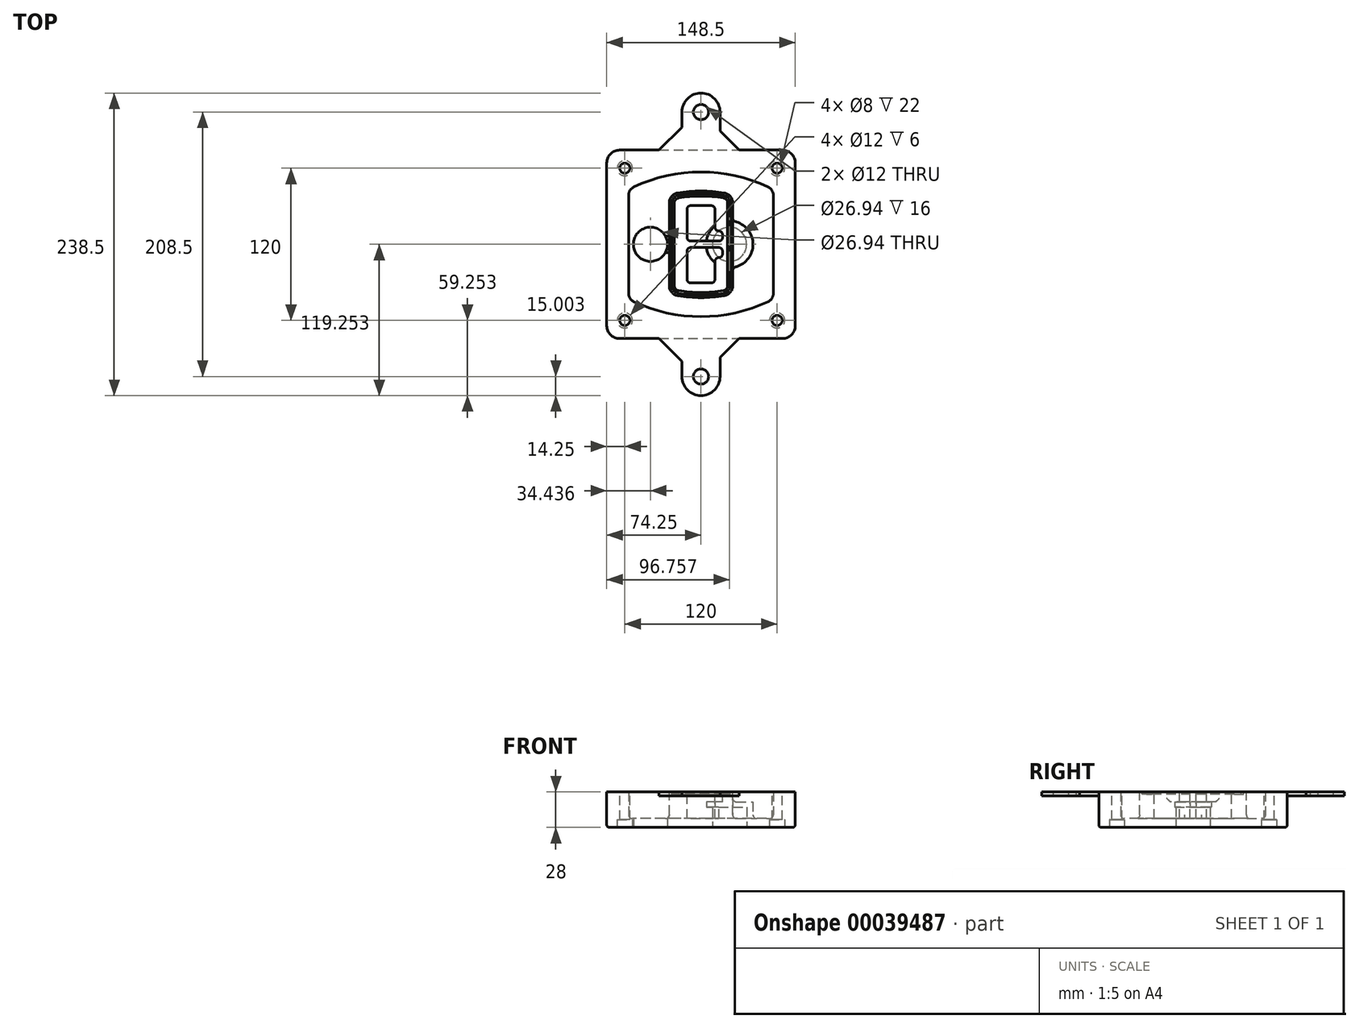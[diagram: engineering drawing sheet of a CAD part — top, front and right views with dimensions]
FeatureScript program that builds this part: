
annotation { "Feature Type Name" : "Feature", "Feature Type Description" : "" }
export const myFeature = defineFeature(function(context is Context, id is Id, definition is map)
    precondition{}
    {
        {
            var Q0;
            Q0=qCreatedBy(makeId("Top.planeOp"),FACE);
            var sketch = newSketch(context, id + "F0", { "sketchPlane" : qUnion([Q0])});
            skPoint(sketch, "E0.rect.middle", {"position": v(0, 0) * mm});
            skLineSegment(sketch, "E1.bottom", {"start": v(24.05, 28.38) * mm, "end": v(152.55, 28.38) * mm});
            skLineSegment(sketch, "E1.top", {"start": v(24.05, 176.88) * mm, "end": v(152.55, 176.88) * mm});
            skLineSegment(sketch, "E1.left", {"start": v(14.05, 38.38) * mm, "end": v(14.05, 166.88) * mm});
            skLineSegment(sketch, "E1.right", {"start": v(162.55, 38.38) * mm, "end": v(162.55, 166.88) * mm});
            skLineSegment(sketch, "E2", {"start": v(14.05, 176.88) * mm, "end": v(162.55, 28.38) * mm, "construction": true});
            skLineSegment(sketch, "E3", {"start": v(162.55, 176.88) * mm, "end": v(14.05, 28.38) * mm, "construction": true});
            skCircle(sketch, "E4", {"center": v(28.3, 162.63) * mm, "radius": 4 * mm});
            skCircle(sketch, "E5", {"center": v(148.3, 162.63) * mm, "radius": 4 * mm});
            skCircle(sketch, "E6", {"center": v(148.3, 42.63) * mm, "radius": 4 * mm});
            skCircle(sketch, "E7", {"center": v(28.3, 42.63) * mm, "radius": 4 * mm});
            skLineSegment(sketch, "E8", {"start": v(28.3, 162.63) * mm, "end": v(148.3, 162.63) * mm, "construction": true});
            skLineSegment(sketch, "E9", {"start": v(148.3, 162.63) * mm, "end": v(148.3, 42.63) * mm, "construction": true});
            skLineSegment(sketch, "E10", {"start": v(148.3, 42.63) * mm, "end": v(28.3, 42.63) * mm, "construction": true});
            skLineSegment(sketch, "E11", {"start": v(28.3, 42.63) * mm, "end": v(28.3, 162.63) * mm, "construction": true});
            skLineSegment(sketch, "E12", {"start": v(28.3, 141.46) * mm, "end": v(28.3, 63.8) * mm});
            skLineSegment(sketch, "E13", {"start": v(148.3, 141.46) * mm, "end": v(148.3, 63.8) * mm});
            skArc(sketch, "E14", {"start": v(142.56, 150.51) * mm, "mid": v(88.3, 162.63) * mm, "end": v(34.04, 150.51) * mm});
            skArc(sketch, "E15", {"start": v(34.04, 54.75) * mm, "mid": v(88.3, 42.63) * mm, "end": v(142.56, 54.75) * mm});
            skLineSegment(sketch, "E16", {"start": v(28.3, 102.63) * mm, "end": v(148.3, 102.63) * mm, "construction": true});
            skPoint(sketch, "E17.visualSharp", {"position": v(28.3, 57.63) * mm});
            skArc(sketch, "E17.filletArc", {"start": v(28.3, 63.8) * mm, "mid": v(29.86, 58.44) * mm, "end": v(34.04, 54.75) * mm});
            skPoint(sketch, "E18.visualSharp", {"position": v(28.3, 147.63) * mm});
            skArc(sketch, "E18.filletArc", {"start": v(34.04, 150.51) * mm, "mid": v(29.86, 146.82) * mm, "end": v(28.3, 141.46) * mm});
            skPoint(sketch, "E19.visualSharp", {"position": v(148.3, 147.63) * mm});
            skArc(sketch, "E19.filletArc", {"start": v(148.3, 141.46) * mm, "mid": v(146.74, 146.82) * mm, "end": v(142.56, 150.51) * mm});
            skPoint(sketch, "E20.visualSharp", {"position": v(148.3, 57.63) * mm});
            skArc(sketch, "E20.filletArc", {"start": v(142.56, 54.75) * mm, "mid": v(146.74, 58.44) * mm, "end": v(148.3, 63.8) * mm});
            skPoint(sketch, "E21.visualSharp", {"position": v(14.05, 176.88) * mm});
            skArc(sketch, "E21.filletArc", {"start": v(24.05, 176.88) * mm, "mid": v(16.98, 173.95) * mm, "end": v(14.05, 166.88) * mm});
            skPoint(sketch, "E22.visualSharp", {"position": v(162.55, 176.88) * mm});
            skArc(sketch, "E22.filletArc", {"start": v(162.55, 166.88) * mm, "mid": v(159.62, 173.95) * mm, "end": v(152.55, 176.88) * mm});
            skPoint(sketch, "E23.visualSharp", {"position": v(162.55, 28.38) * mm});
            skArc(sketch, "E23.filletArc", {"start": v(152.55, 28.38) * mm, "mid": v(159.62, 31.31) * mm, "end": v(162.55, 38.38) * mm});
            skPoint(sketch, "E24.visualSharp", {"position": v(14.05, 28.38) * mm});
            skArc(sketch, "E24.filletArc", {"start": v(14.05, 38.38) * mm, "mid": v(16.98, 31.31) * mm, "end": v(24.05, 28.38) * mm});
            skArc(sketch, "E25.0", {"start": v(145.3, 141.46) * mm, "mid": v(144.2, 145.22) * mm, "end": v(141.28, 147.8) * mm});
            skLineSegment(sketch, "E25.1", {"start": v(145.3, 141.46) * mm, "end": v(145.3, 63.8) * mm});
            skArc(sketch, "E25.2", {"start": v(141.28, 57.47) * mm, "mid": v(144.2, 60.05) * mm, "end": v(145.3, 63.8) * mm});
            skArc(sketch, "E25.3", {"start": v(35.32, 57.47) * mm, "mid": v(88.3, 45.63) * mm, "end": v(141.28, 57.47) * mm});
            skArc(sketch, "E25.4", {"start": v(31.3, 63.8) * mm, "mid": v(32.4, 60.05) * mm, "end": v(35.32, 57.47) * mm});
            skArc(sketch, "E25.5", {"start": v(141.28, 147.8) * mm, "mid": v(88.3, 159.63) * mm, "end": v(35.32, 147.8) * mm});
            skLineSegment(sketch, "E25.6", {"start": v(31.3, 141.46) * mm, "end": v(31.3, 63.8) * mm});
            skArc(sketch, "E25.7", {"start": v(35.32, 147.8) * mm, "mid": v(32.4, 145.22) * mm, "end": v(31.3, 141.46) * mm});
            skArc(sketch, "E26.0", {"start": v(32.34, 154.13) * mm, "mid": v(26.48, 148.97) * mm, "end": v(24.3, 141.46) * mm});
            skArc(sketch, "E26.1", {"start": v(144.26, 154.13) * mm, "mid": v(88.3, 166.63) * mm, "end": v(32.34, 154.13) * mm});
            skArc(sketch, "E26.2", {"start": v(152.3, 141.46) * mm, "mid": v(150.12, 148.97) * mm, "end": v(144.26, 154.13) * mm});
            skLineSegment(sketch, "E26.3", {"start": v(152.3, 141.46) * mm, "end": v(152.3, 63.8) * mm});
            skArc(sketch, "E26.4", {"start": v(144.26, 51.13) * mm, "mid": v(150.12, 56.3) * mm, "end": v(152.3, 63.8) * mm});
            skLineSegment(sketch, "E26.5", {"start": v(24.3, 141.46) * mm, "end": v(24.3, 63.8) * mm});
            skArc(sketch, "E26.6", {"start": v(32.34, 51.13) * mm, "mid": v(88.3, 38.63) * mm, "end": v(144.26, 51.13) * mm});
            skArc(sketch, "E26.7", {"start": v(24.3, 63.8) * mm, "mid": v(26.48, 56.3) * mm, "end": v(32.34, 51.13) * mm});
            skSolve(sketch);
        }
        {
            var Q0;
            Q0=makeQuery(id+"F0.imprint","IMPRINT",FACE,{"disambiguationData":[TD([[makeQuery(id+"F0.imprint","IMPRINT",EDGE,{"derivedFrom":sQuery(id+"F0.wireOp",EDGE,"E1.bottom")}),1.0]])]});
            var Q1;
            Q1=makeQuery(id+"F0.imprint","IMPRINT",FACE,{"disambiguationData":[TD([[makeQuery(id+"F0.imprint","IMPRINT",EDGE,{"derivedFrom":sQuery(id+"F0.wireOp",EDGE,"E12")}),1.0]])]});
            var Q2;
            Q2=makeQuery(id+"F0.imprint","IMPRINT",FACE,{"disambiguationData":[TD([[makeQuery(id+"F0.imprint","IMPRINT",EDGE,{"derivedFrom":sQuery(id+"F0.wireOp",EDGE,"E25.0")}),1.0]])]});
            var Q3;
            Q3=makeQuery(id+"F0.imprint","IMPRINT",FACE,{"disambiguationData":[TD([[makeQuery(id+"F0.imprint","IMPRINT",EDGE,{"derivedFrom":sQuery(id+"F0.wireOp",EDGE,"E12")}),-1.0]])]});
            extrude(context, id + "F1", {"entities" : qUnion([Q0, Q1, Q2, Q3]), "oppositeDirection" : true, "depth" : 25 * mm});
        }
        {
            var Q0;
            Q0=makeQuery(id+"F0.imprint","IMPRINT",FACE,{"disambiguationData":[TD([[makeQuery(id+"F0.imprint","IMPRINT",EDGE,{"derivedFrom":sQuery(id+"F0.wireOp",EDGE,"E12")}),1.0]])]});
            extrude(context, id + "F2", {"entities" : qUnion([Q0]), "operationType" : NewBodyOperationType.ADD, "depth" : 3 * mm});
        }
        {
            var Q0;
            Q0=makeQuery(id+"F0.imprint","IMPRINT",FACE,{"disambiguationData":[TD([[makeQuery(id+"F0.imprint","IMPRINT",EDGE,{"derivedFrom":sQuery(id+"F0.wireOp",EDGE,"E25.0")}),1.0]])]});
            extrude(context, id + "F3", {"entities" : qUnion([Q0]), "operationType" : NewBodyOperationType.REMOVE, "oppositeDirection" : true, "depth" : 18 * mm});
        }
        {
            var Q0;
            Q0=makeQuery(id+"F2.opExtrude","CAP_FACE",FACE,{"disambiguationData":[OSD([sQuery(id+"F0.wireOp",EDGE,"E12"),sQuery(id+"F0.wireOp",EDGE,"E13"),sQuery(id+"F0.wireOp",EDGE,"E14"),sQuery(id+"F0.wireOp",EDGE,"E15"),sQuery(id+"F0.wireOp",EDGE,"E17.filletArc"),sQuery(id+"F0.wireOp",EDGE,"E18.filletArc"),sQuery(id+"F0.wireOp",EDGE,"E19.filletArc"),sQuery(id+"F0.wireOp",EDGE,"E20.filletArc"),sQuery(id+"F0.wireOp",EDGE,"E25.0"),sQuery(id+"F0.wireOp",EDGE,"E25.1"),sQuery(id+"F0.wireOp",EDGE,"E25.2"),sQuery(id+"F0.wireOp",EDGE,"E25.3"),sQuery(id+"F0.wireOp",EDGE,"E25.4"),sQuery(id+"F0.wireOp",EDGE,"E25.5"),sQuery(id+"F0.wireOp",EDGE,"E25.6"),sQuery(id+"F0.wireOp",EDGE,"E25.7")])],"isStart":false});
            var sketch = newSketch(context, id + "F4", { "sketchPlane" : qUnion([Q0])});
            skArc(sketch, "E27.0", {"start": v(69.96, 62.18) * mm, "mid": v(88.3, 60.63) * mm, "end": v(106.64, 62.18) * mm});
            skArc(sketch, "E28.0", {"start": v(106.64, 143.09) * mm, "mid": v(88.3, 144.63) * mm, "end": v(69.96, 143.09) * mm});
            skLineSegment(sketch, "E29", {"start": v(63.3, 135.2) * mm, "end": v(63.3, 70.07) * mm});
            skLineSegment(sketch, "E30", {"start": v(113.3, 135.2) * mm, "end": v(113.3, 70.07) * mm});
            skLineSegment(sketch, "E31", {"start": v(63.3, 141.74) * mm, "end": v(113.3, 141.74) * mm, "construction": true});
            skLineSegment(sketch, "E32", {"start": v(63.3, 63.52) * mm, "end": v(113.3, 63.52) * mm, "construction": true});
            skPoint(sketch, "E33.visualSharp", {"position": v(63.3, 141.74) * mm});
            skArc(sketch, "E33.filletArc", {"start": v(69.96, 143.09) * mm, "mid": v(65.19, 140.36) * mm, "end": v(63.3, 135.2) * mm});
            skPoint(sketch, "E34.visualSharp", {"position": v(113.3, 141.74) * mm});
            skArc(sketch, "E34.filletArc", {"start": v(113.3, 135.2) * mm, "mid": v(111.41, 140.36) * mm, "end": v(106.64, 143.09) * mm});
            skPoint(sketch, "E35.visualSharp", {"position": v(113.3, 63.52) * mm});
            skArc(sketch, "E35.filletArc", {"start": v(106.64, 62.18) * mm, "mid": v(111.41, 64.9) * mm, "end": v(113.3, 70.07) * mm});
            skPoint(sketch, "E36.visualSharp", {"position": v(63.3, 63.52) * mm});
            skArc(sketch, "E36.filletArc", {"start": v(63.3, 70.07) * mm, "mid": v(65.19, 64.9) * mm, "end": v(69.96, 62.18) * mm});
            skArc(sketch, "E37.0", {"start": v(141.28, 147.8) * mm, "mid": v(88.3, 159.63) * mm, "end": v(35.32, 147.8) * mm});
            skArc(sketch, "E37.1", {"start": v(35.32, 147.8) * mm, "mid": v(32.4, 145.22) * mm, "end": v(31.3, 141.46) * mm});
            skLineSegment(sketch, "E37.2", {"start": v(31.3, 141.46) * mm, "end": v(31.3, 63.8) * mm});
            skArc(sketch, "E37.3", {"start": v(31.3, 63.8) * mm, "mid": v(32.4, 60.05) * mm, "end": v(35.32, 57.47) * mm});
            skArc(sketch, "E37.4", {"start": v(35.32, 57.47) * mm, "mid": v(88.3, 45.63) * mm, "end": v(141.28, 57.47) * mm});
            skArc(sketch, "E37.5", {"start": v(141.28, 57.47) * mm, "mid": v(144.2, 60.05) * mm, "end": v(145.3, 63.8) * mm});
            skLineSegment(sketch, "E37.6", {"start": v(145.3, 141.46) * mm, "end": v(145.3, 63.8) * mm});
            skArc(sketch, "E37.7", {"start": v(145.3, 141.46) * mm, "mid": v(144.2, 145.22) * mm, "end": v(141.28, 147.8) * mm});
            skLineSegment(sketch, "E38.0", {"start": v(111.3, 135.2) * mm, "end": v(111.3, 70.07) * mm});
            skArc(sketch, "E38.1", {"start": v(106.3, 64.15) * mm, "mid": v(109.88, 66.2) * mm, "end": v(111.3, 70.07) * mm});
            skArc(sketch, "E38.2", {"start": v(70.3, 64.15) * mm, "mid": v(88.3, 62.63) * mm, "end": v(106.3, 64.15) * mm});
            skArc(sketch, "E38.3", {"start": v(65.3, 70.07) * mm, "mid": v(66.72, 66.2) * mm, "end": v(70.3, 64.15) * mm});
            skLineSegment(sketch, "E38.4", {"start": v(65.3, 135.2) * mm, "end": v(65.3, 70.07) * mm});
            skArc(sketch, "E38.5", {"start": v(111.3, 135.2) * mm, "mid": v(109.88, 139.07) * mm, "end": v(106.3, 141.11) * mm});
            skArc(sketch, "E38.6", {"start": v(70.3, 141.11) * mm, "mid": v(66.72, 139.07) * mm, "end": v(65.3, 135.2) * mm});
            skArc(sketch, "E38.7", {"start": v(106.3, 141.11) * mm, "mid": v(88.3, 142.63) * mm, "end": v(70.3, 141.11) * mm});
            skArc(sketch, "E39.0", {"start": v(109.3, 135.2) * mm, "mid": v(108.36, 137.78) * mm, "end": v(105.97, 139.14) * mm});
            skLineSegment(sketch, "E39.1", {"start": v(109.3, 135.2) * mm, "end": v(109.3, 70.07) * mm});
            skArc(sketch, "E39.2", {"start": v(105.97, 66.12) * mm, "mid": v(108.36, 67.49) * mm, "end": v(109.3, 70.07) * mm});
            skArc(sketch, "E39.3", {"start": v(70.63, 66.12) * mm, "mid": v(88.3, 64.63) * mm, "end": v(105.97, 66.12) * mm});
            skArc(sketch, "E39.4", {"start": v(67.3, 70.07) * mm, "mid": v(68.24, 67.49) * mm, "end": v(70.63, 66.12) * mm});
            skArc(sketch, "E39.5", {"start": v(105.97, 139.14) * mm, "mid": v(88.3, 140.63) * mm, "end": v(70.63, 139.14) * mm});
            skLineSegment(sketch, "E39.6", {"start": v(67.3, 135.2) * mm, "end": v(67.3, 70.07) * mm});
            skArc(sketch, "E39.7", {"start": v(70.63, 139.14) * mm, "mid": v(68.24, 137.78) * mm, "end": v(67.3, 135.2) * mm});
            skLineSegment(sketch, "E40", {"start": v(63.3, 102.63) * mm, "end": v(113.3, 102.63) * mm, "construction": true});
            skLineSegment(sketch, "E41", {"start": v(77.3, 108.13) * mm, "end": v(77.3, 130.13) * mm});
            skLineSegment(sketch, "E42", {"start": v(80.3, 133.13) * mm, "end": v(96.3, 133.13) * mm});
            skLineSegment(sketch, "E43", {"start": v(99.3, 130.13) * mm, "end": v(99.3, 116.13) * mm});
            skLineSegment(sketch, "E44", {"start": v(102.3, 113.13) * mm, "end": v(102.3, 113.13) * mm});
            skLineSegment(sketch, "E45", {"start": v(105.3, 110.13) * mm, "end": v(105.3, 108.13) * mm});
            skLineSegment(sketch, "E46", {"start": v(102.3, 105.13) * mm, "end": v(80.3, 105.13) * mm});
            skPoint(sketch, "E47.visualSharp", {"position": v(77.3, 133.13) * mm});
            skArc(sketch, "E47.filletArc", {"start": v(80.3, 133.13) * mm, "mid": v(78.18, 132.25) * mm, "end": v(77.3, 130.13) * mm});
            skPoint(sketch, "E48.visualSharp", {"position": v(99.3, 133.13) * mm});
            skArc(sketch, "E48.filletArc", {"start": v(99.3, 130.13) * mm, "mid": v(98.42, 132.25) * mm, "end": v(96.3, 133.13) * mm});
            skPoint(sketch, "E49.visualSharp", {"position": v(99.3, 113.13) * mm});
            skArc(sketch, "E49.filletArc", {"start": v(99.3, 116.13) * mm, "mid": v(100.18, 114.01) * mm, "end": v(102.3, 113.13) * mm});
            skPoint(sketch, "E50.visualSharp", {"position": v(105.3, 113.13) * mm});
            skArc(sketch, "E50.filletArc", {"start": v(105.3, 110.13) * mm, "mid": v(104.42, 112.25) * mm, "end": v(102.3, 113.13) * mm});
            skPoint(sketch, "E51.visualSharp", {"position": v(105.3, 105.13) * mm});
            skArc(sketch, "E51.filletArc", {"start": v(102.3, 105.13) * mm, "mid": v(104.42, 106.01) * mm, "end": v(105.3, 108.13) * mm});
            skPoint(sketch, "E52.visualSharp", {"position": v(77.3, 105.13) * mm});
            skArc(sketch, "E52.filletArc", {"start": v(77.3, 108.13) * mm, "mid": v(78.18, 106.01) * mm, "end": v(80.3, 105.13) * mm});
            skLineSegment(sketch, "E53.0.MirrorCS", {"start": v(102.3, 100.13) * mm, "end": v(80.3, 100.13) * mm});
            skArc(sketch, "E54.0.MirrorCS", {"start": v(77.3, 97.13) * mm, "mid": v(78.18, 99.25) * mm, "end": v(80.3, 100.13) * mm});
            skLineSegment(sketch, "E55.0.MirrorCS", {"start": v(77.3, 97.13) * mm, "end": v(77.3, 75.13) * mm});
            skArc(sketch, "E56.0.MirrorCS", {"start": v(80.3, 72.13) * mm, "mid": v(78.18, 73.01) * mm, "end": v(77.3, 75.13) * mm});
            skLineSegment(sketch, "E57.0.MirrorCS", {"start": v(80.3, 72.13) * mm, "end": v(96.3, 72.13) * mm});
            skArc(sketch, "E58.0.MirrorCS", {"start": v(99.3, 75.13) * mm, "mid": v(98.42, 73.01) * mm, "end": v(96.3, 72.13) * mm});
            skLineSegment(sketch, "E59.0.MirrorCS", {"start": v(99.3, 75.13) * mm, "end": v(99.3, 89.13) * mm});
            skArc(sketch, "E60.0.MirrorCS", {"start": v(99.3, 89.13) * mm, "mid": v(100.18, 91.25) * mm, "end": v(102.3, 92.13) * mm});
            skArc(sketch, "E61.0.MirrorCS", {"start": v(105.3, 95.13) * mm, "mid": v(104.42, 93.01) * mm, "end": v(102.3, 92.13) * mm});
            skLineSegment(sketch, "E62.0.MirrorCS", {"start": v(105.3, 95.13) * mm, "end": v(105.3, 97.13) * mm});
            skArc(sketch, "E63.0.MirrorCS", {"start": v(102.3, 100.13) * mm, "mid": v(104.42, 99.25) * mm, "end": v(105.3, 97.13) * mm});
            skSolve(sketch);
        }
        {
            var Q0;
            Q0=makeQuery(id+"F4.imprint","IMPRINT",FACE,{"disambiguationData":[TD([[makeQuery(id+"F4.imprint","IMPRINT",EDGE,{"derivedFrom":sQuery(id+"F4.wireOp",EDGE,"E27.0")}),1.0]])]});
            var Q1;
            Q1=makeQuery(id+"F4.imprint","IMPRINT",FACE,{"disambiguationData":[TD([[makeQuery(id+"F4.imprint","IMPRINT",EDGE,{"derivedFrom":sQuery(id+"F4.wireOp",EDGE,"E38.0")}),-1.0]])]});
            var Q2;
            Q2=makeQuery(id+"F4.imprint","IMPRINT",FACE,{"disambiguationData":[TD([[makeQuery(id+"F4.imprint","IMPRINT",EDGE,{"derivedFrom":sQuery(id+"F4.wireOp",EDGE,"E39.0")}),1.0]])]});
            extrude(context, id + "F5", {"entities" : qUnion([Q0, Q1, Q2]), "operationType" : NewBodyOperationType.ADD, "endBound" : BoundingType.UP_TO_NEXT, "oppositeDirection" : true, "depth" : 25 * mm});
        }
        {
            var Q0;
            Q0=makeQuery(id+"F4.imprint","IMPRINT",FACE,{"disambiguationData":[TD([[makeQuery(id+"F4.imprint","IMPRINT",EDGE,{"derivedFrom":sQuery(id+"F4.wireOp",EDGE,"E38.0")}),-1.0]])]});
            extrude(context, id + "F6", {"entities" : qUnion([Q0]), "operationType" : NewBodyOperationType.REMOVE, "oppositeDirection" : true, "depth" : 2 * mm});
        }
        {
            var Q0;
            Q0=makeQuery(id+"F1.opExtrude","CAP_FACE",FACE,{"disambiguationData":[OSD([sQuery(id+"F0.wireOp",EDGE,"E1.bottom"),sQuery(id+"F0.wireOp",EDGE,"E1.top"),sQuery(id+"F0.wireOp",EDGE,"E1.left"),sQuery(id+"F0.wireOp",EDGE,"E1.right"),sQuery(id+"F0.wireOp",EDGE,"E4"),sQuery(id+"F0.wireOp",EDGE,"E5"),sQuery(id+"F0.wireOp",EDGE,"E6"),sQuery(id+"F0.wireOp",EDGE,"E7"),sQuery(id+"F0.wireOp",EDGE,"E21.filletArc"),sQuery(id+"F0.wireOp",EDGE,"E22.filletArc"),sQuery(id+"F0.wireOp",EDGE,"E23.filletArc"),sQuery(id+"F0.wireOp",EDGE,"E24.filletArc")])],"isStart":false});
            var sketch = newSketch(context, id + "F7", { "sketchPlane" : qUnion([Q0])});
            skCircle(sketch, "E64", {"center": v(110.8, -102.63) * mm, "radius": 13.47 * mm});
            skCircle(sketch, "E65", {"center": v(48.49, -102.63) * mm, "radius": 13.47 * mm});
            skLineSegment(sketch, "E66", {"start": v(162.55, -102.63) * mm, "end": v(14.05, -102.63) * mm});
            skCircle(sketch, "E67", {"center": v(110.8, -102.63) * mm, "radius": 18.47 * mm});
            skCircle(sketch, "E68", {"center": v(148.3, -162.63) * mm, "radius": 6 * mm});
            skCircle(sketch, "E69", {"center": v(28.3, -162.63) * mm, "radius": 6 * mm});
            skCircle(sketch, "E70", {"center": v(28.3, -42.63) * mm, "radius": 6 * mm});
            skCircle(sketch, "E71", {"center": v(148.3, -42.63) * mm, "radius": 6 * mm});
            skSolve(sketch);
        }
        {
            var Q0;
            {var subQ1=sQuery(id+"F7.wireOp",EDGE,"E66");var subQ4=sQuery(id+"F7.wireOp",EDGE,"E64");var subQ6=makeQuery(id+"F7.imprint","INTERSECT",VERTEX,{"disambiguationData":[OD(0.0)],"derivedFrom":[subQ4,subQ1]});Q0=makeQuery(id+"F7.imprint","IMPRINT",FACE,{"disambiguationData":[TD([[makeQuery(id+"F7.imprint","IMPRINT",EDGE,{"disambiguationData":[TD([[subQ6,-1.0]])],"derivedFrom":subQ4}),-1.0]])]});}
            var Q1;
            {var subQ0=sQuery(id+"F7.wireOp",EDGE,"E66");var subQ1=sQuery(id+"F7.wireOp",EDGE,"E64");var subQ3=makeQuery(id+"F7.imprint","INTERSECT",VERTEX,{"disambiguationData":[OD(0.0)],"derivedFrom":[subQ1,subQ0]});Q1=makeQuery(id+"F7.imprint","IMPRINT",FACE,{"disambiguationData":[TD([[makeQuery(id+"F7.imprint","IMPRINT",EDGE,{"disambiguationData":[TD([[subQ3,-1.0]])],"derivedFrom":subQ1}),1.0]])]});}
            var Q2;
            {var subQ0=sQuery(id+"F7.wireOp",EDGE,"E66");var subQ1=sQuery(id+"F7.wireOp",EDGE,"E64");var subQ3=makeQuery(id+"F7.imprint","INTERSECT",VERTEX,{"disambiguationData":[OD(0.0)],"derivedFrom":[subQ1,subQ0]});Q2=makeQuery(id+"F7.imprint","IMPRINT",FACE,{"disambiguationData":[TD([[makeQuery(id+"F7.imprint","IMPRINT",EDGE,{"disambiguationData":[TD([[subQ3,1.0]])],"derivedFrom":subQ1}),1.0]])]});}
            var Q3;
            {var subQ1=sQuery(id+"F7.wireOp",EDGE,"E66");var subQ4=sQuery(id+"F7.wireOp",EDGE,"E64");var subQ6=makeQuery(id+"F7.imprint","INTERSECT",VERTEX,{"disambiguationData":[OD(0.0)],"derivedFrom":[subQ4,subQ1]});Q3=makeQuery(id+"F7.imprint","IMPRINT",FACE,{"disambiguationData":[TD([[makeQuery(id+"F7.imprint","IMPRINT",EDGE,{"disambiguationData":[TD([[subQ6,1.0]])],"derivedFrom":subQ4}),-1.0]])]});}
            extrude(context, id + "F8", {"entities" : qUnion([Q0, Q1, Q2, Q3]), "operationType" : NewBodyOperationType.ADD, "oppositeDirection" : true, "depth" : 20 * mm});
        }
        {
            var Q0;
            {var subQ0=sQuery(id+"F7.wireOp",EDGE,"E66");var subQ1=sQuery(id+"F7.wireOp",EDGE,"E64");var subQ3=makeQuery(id+"F7.imprint","INTERSECT",VERTEX,{"disambiguationData":[OD(0.0)],"derivedFrom":[subQ1,subQ0]});Q0=makeQuery(id+"F7.imprint","IMPRINT",FACE,{"disambiguationData":[TD([[makeQuery(id+"F7.imprint","IMPRINT",EDGE,{"disambiguationData":[TD([[subQ3,-1.0]])],"derivedFrom":subQ1}),1.0]])]});}
            var Q1;
            {var subQ0=sQuery(id+"F7.wireOp",EDGE,"E66");var subQ1=sQuery(id+"F7.wireOp",EDGE,"E64");var subQ3=makeQuery(id+"F7.imprint","INTERSECT",VERTEX,{"disambiguationData":[OD(0.0)],"derivedFrom":[subQ1,subQ0]});Q1=makeQuery(id+"F7.imprint","IMPRINT",FACE,{"disambiguationData":[TD([[makeQuery(id+"F7.imprint","IMPRINT",EDGE,{"disambiguationData":[TD([[subQ3,1.0]])],"derivedFrom":subQ1}),1.0]])]});}
            extrude(context, id + "F9", {"entities" : qUnion([Q0, Q1]), "operationType" : NewBodyOperationType.REMOVE, "oppositeDirection" : true, "depth" : 16 * mm});
        }
        {
            var Q0;
            {var subQ0=sQuery(id+"F7.wireOp",EDGE,"E66");var subQ1=sQuery(id+"F7.wireOp",EDGE,"E65");var subQ3=makeQuery(id+"F7.imprint","INTERSECT",VERTEX,{"disambiguationData":[OD(0.0)],"derivedFrom":[subQ1,subQ0]});Q0=makeQuery(id+"F7.imprint","IMPRINT",FACE,{"disambiguationData":[TD([[makeQuery(id+"F7.imprint","IMPRINT",EDGE,{"disambiguationData":[TD([[subQ3,-1.0]])],"derivedFrom":subQ1}),1.0]])]});}
            var Q1;
            {var subQ0=sQuery(id+"F7.wireOp",EDGE,"E66");var subQ1=sQuery(id+"F7.wireOp",EDGE,"E65");var subQ3=makeQuery(id+"F7.imprint","INTERSECT",VERTEX,{"disambiguationData":[OD(0.0)],"derivedFrom":[subQ1,subQ0]});Q1=makeQuery(id+"F7.imprint","IMPRINT",FACE,{"disambiguationData":[TD([[makeQuery(id+"F7.imprint","IMPRINT",EDGE,{"disambiguationData":[TD([[subQ3,1.0]])],"derivedFrom":subQ1}),1.0]])]});}
            extrude(context, id + "F10", {"entities" : qUnion([Q0, Q1]), "operationType" : NewBodyOperationType.REMOVE, "oppositeDirection" : true, "depth" : 25 * mm});
        }
        {
            var Q0;
            Q0=makeQuery(id+"F7.imprint","IMPRINT",FACE,{"disambiguationData":[TD([[makeQuery(id+"F7.imprint","IMPRINT",EDGE,{"derivedFrom":sQuery(id+"F7.wireOp",EDGE,"E68")}),1.0]])]});
            var Q1;
            Q1=makeQuery(id+"F7.imprint","IMPRINT",FACE,{"disambiguationData":[TD([[makeQuery(id+"F7.imprint","IMPRINT",EDGE,{"derivedFrom":makeQuery(id+"F1.opExtrude","CAP_EDGE",EDGE,{"disambiguationData":[OSD([sQuery(id+"F0.wireOp",EDGE,"E5")])],"isStart":false})}),-1.0]])]});
            var Q2;
            Q2=makeQuery(id+"F7.imprint","IMPRINT",FACE,{"disambiguationData":[TD([[makeQuery(id+"F7.imprint","IMPRINT",EDGE,{"derivedFrom":sQuery(id+"F7.wireOp",EDGE,"E69")}),1.0]])]});
            var Q3;
            Q3=makeQuery(id+"F7.imprint","IMPRINT",FACE,{"disambiguationData":[TD([[makeQuery(id+"F7.imprint","IMPRINT",EDGE,{"derivedFrom":makeQuery(id+"F1.opExtrude","CAP_EDGE",EDGE,{"disambiguationData":[OSD([sQuery(id+"F0.wireOp",EDGE,"E4")])],"isStart":false})}),-1.0]])]});
            var Q4;
            Q4=makeQuery(id+"F7.imprint","IMPRINT",FACE,{"disambiguationData":[TD([[makeQuery(id+"F7.imprint","IMPRINT",EDGE,{"derivedFrom":sQuery(id+"F7.wireOp",EDGE,"E70")}),1.0]])]});
            var Q5;
            Q5=makeQuery(id+"F7.imprint","IMPRINT",FACE,{"disambiguationData":[TD([[makeQuery(id+"F7.imprint","IMPRINT",EDGE,{"derivedFrom":makeQuery(id+"F1.opExtrude","CAP_EDGE",EDGE,{"disambiguationData":[OSD([sQuery(id+"F0.wireOp",EDGE,"E7")])],"isStart":false})}),-1.0]])]});
            var Q6;
            Q6=makeQuery(id+"F7.imprint","IMPRINT",FACE,{"disambiguationData":[TD([[makeQuery(id+"F7.imprint","IMPRINT",EDGE,{"derivedFrom":sQuery(id+"F7.wireOp",EDGE,"E71")}),1.0]])]});
            var Q7;
            Q7=makeQuery(id+"F7.imprint","IMPRINT",FACE,{"disambiguationData":[TD([[makeQuery(id+"F7.imprint","IMPRINT",EDGE,{"derivedFrom":makeQuery(id+"F1.opExtrude","CAP_EDGE",EDGE,{"disambiguationData":[OSD([sQuery(id+"F0.wireOp",EDGE,"E6")])],"isStart":false})}),-1.0]])]});
            extrude(context, id + "F11", {"entities" : qUnion([Q0, Q1, Q2, Q3, Q4, Q5, Q6, Q7]), "operationType" : NewBodyOperationType.REMOVE, "oppositeDirection" : true, "depth" : 6 * mm});
        }
        {
            var Q0;
            Q0=makeQuery(id+"F9.boolean.opBoolean","COPY",FACE,{"derivedFrom":makeQuery(id+"F9.opExtrude","CAP_FACE",FACE,{"disambiguationData":[OSD([sQuery(id+"F7.wireOp",EDGE,"E64")])],"isStart":false})});
            var sketch = newSketch(context, id + "F12", { "sketchPlane" : qUnion([Q0])});
            skArc(sketch, "E72.0", {"start": v(99.3, -88.19) * mm, "mid": v(94.75, -93.5) * mm, "end": v(92.5, -100.13) * mm});
            skArc(sketch, "E72.1", {"start": v(92.5, -105.13) * mm, "mid": v(94.75, -111.76) * mm, "end": v(99.3, -117.08) * mm});
            skLineSegment(sketch, "E73", {"start": v(92.5, -105.13) * mm, "end": v(102.3, -105.13) * mm});
            skLineSegment(sketch, "E74.0", {"start": v(102.3, -100.13) * mm, "end": v(92.5, -100.13) * mm});
            skArc(sketch, "E74.1", {"start": v(102.3, -100.13) * mm, "mid": v(104.42, -99.25) * mm, "end": v(105.3, -97.13) * mm});
            skLineSegment(sketch, "E74.2", {"start": v(105.3, -95.13) * mm, "end": v(105.3, -97.13) * mm});
            skArc(sketch, "E74.3", {"start": v(105.3, -95.13) * mm, "mid": v(104.42, -93.01) * mm, "end": v(102.3, -92.13) * mm});
            skArc(sketch, "E74.4", {"start": v(99.3, -89.13) * mm, "mid": v(100.18, -91.25) * mm, "end": v(102.3, -92.13) * mm});
            skLineSegment(sketch, "E74.5", {"start": v(99.3, -88.19) * mm, "end": v(99.3, -89.13) * mm});
            skLineSegment(sketch, "E74.7", {"start": v(102.3, -105.13) * mm, "end": v(92.5, -105.13) * mm});
            skArc(sketch, "E74.8", {"start": v(102.3, -105.13) * mm, "mid": v(104.42, -106.01) * mm, "end": v(105.3, -108.13) * mm});
            skLineSegment(sketch, "E74.9", {"start": v(105.3, -110.13) * mm, "end": v(105.3, -108.13) * mm});
            skArc(sketch, "E74.10", {"start": v(105.3, -110.13) * mm, "mid": v(104.42, -112.25) * mm, "end": v(102.3, -113.13) * mm});
            skArc(sketch, "E74.11", {"start": v(99.3, -116.13) * mm, "mid": v(100.18, -114.01) * mm, "end": v(102.3, -113.13) * mm});
            skLineSegment(sketch, "E74.12", {"start": v(99.3, -117.08) * mm, "end": v(99.3, -116.13) * mm});
            skPoint(sketch, "E75.orphan", {"position": v(99.3, -130.13) * mm});
            skPoint(sketch, "E76.orphan", {"position": v(80.3, -105.13) * mm});
            skPoint(sketch, "E77.orphan", {"position": v(80.3, -100.13) * mm});
            skPoint(sketch, "E78.orphan", {"position": v(99.3, -75.13) * mm});
            skSolve(sketch);
        }
        {
            var Q0;
            {var subQ7=sQuery(id+"F12.wireOp",EDGE,"E72.0");var subQ14=sQuery(id+"F12.wireOp",EDGE,"E72.1");var subQ16=sQuery(id+"F12.wireOp",EDGE,"E74.1");var subQ18=sQuery(id+"F12.wireOp",EDGE,"E74.8");Q0=qUnion([makeQuery(id+"F12.imprint","IMPRINT",FACE,{"disambiguationData":[TD([[makeQuery(id+"F12.imprint","IMPRINT",EDGE,{"derivedFrom":subQ7}),1.0]])]}),makeQuery(id+"F12.imprint","IMPRINT",FACE,{"disambiguationData":[TD([[makeQuery(id+"F12.imprint","IMPRINT",EDGE,{"derivedFrom":subQ14}),1.0]])]}),makeQuery(id+"F12.imprint","IMPRINT",FACE,{"disambiguationData":[TD([[makeQuery(id+"F12.imprint","IMPRINT",EDGE,{"derivedFrom":subQ16}),1.0]])]}),makeQuery(id+"F12.imprint","IMPRINT",FACE,{"disambiguationData":[TD([[makeQuery(id+"F12.imprint","IMPRINT",EDGE,{"derivedFrom":subQ18}),-1.0]])]})]);}
            var Q1;
            Q1=makeQuery(id+"F5.boolean.opBoolean","SPLIT",FACE,{"disambiguationData":[TD([makeQuery(id+"F5.opExtrude","SWEPT_FACE",FACE,{"disambiguationData":[OSD([sQuery(id+"F4.wireOp",EDGE,"E41")])]})])],"derivedFrom":makeQuery(id+"F3.boolean.opBoolean","COPY",FACE,{"derivedFrom":makeQuery(id+"F3.opExtrude","CAP_FACE",FACE,{"disambiguationData":[OSD([sQuery(id+"F0.wireOp",EDGE,"E25.0"),sQuery(id+"F0.wireOp",EDGE,"E25.1"),sQuery(id+"F0.wireOp",EDGE,"E25.2"),sQuery(id+"F0.wireOp",EDGE,"E25.3"),sQuery(id+"F0.wireOp",EDGE,"E25.4"),sQuery(id+"F0.wireOp",EDGE,"E25.5"),sQuery(id+"F0.wireOp",EDGE,"E25.6"),sQuery(id+"F0.wireOp",EDGE,"E25.7")])],"isStart":false})})});
            extrude(context, id + "F13", {"entities" : qUnion([Q0]), "operationType" : NewBodyOperationType.REMOVE, "endBound" : BoundingType.UP_TO_SURFACE, "endBoundEntityFace" : qUnion([Q1]), "depth" : 25 * mm});
        }
        {
            var Q0;
            Q0=makeQuery(id+"F3.boolean.opBoolean","COPY",EDGE,{"derivedFrom":makeQuery(id+"F3.opExtrude","CAP_EDGE",EDGE,{"disambiguationData":[OSD([sQuery(id+"F0.wireOp",EDGE,"E25.6")])],"isStart":false})});
            var Q1;
            Q1=makeQuery(id+"F8.boolean.opBoolean","INTERSECT",EDGE,{"derivedFrom":[makeQuery(id+"F5.opExtrude","SWEPT_FACE",FACE,{"disambiguationData":[OSD([sQuery(id+"F4.wireOp",EDGE,"E30")])]}),makeQuery(id+"F8.opExtrude","CAP_FACE",FACE,{"disambiguationData":[OSD([sQuery(id+"F7.wireOp",EDGE,"E67")])],"isStart":false})]});
            var Q2;
            Q2=makeQuery(id+"F8.boolean.opBoolean","INTERSECT",EDGE,{"disambiguationData":[OD(1.0)],"derivedFrom":[makeQuery(id+"F5.opExtrude","SWEPT_FACE",FACE,{"disambiguationData":[OSD([sQuery(id+"F4.wireOp",EDGE,"E30")])]}),makeQuery(id+"F8.opExtrude","SWEPT_FACE",FACE,{"disambiguationData":[OSD([sQuery(id+"F7.wireOp",EDGE,"E67")])]})]});
            var Q3;
            {var subQ0=sQuery(id+"F4.wireOp",EDGE,"E30");Q3=makeQuery(id+"F8.boolean.opBoolean","SPLIT",EDGE,{"disambiguationData":[TD([makeQuery(id+"F5.opExtrude","SWEPT_FACE",FACE,{"disambiguationData":[OSD([sQuery(id+"F4.wireOp",EDGE,"E35.filletArc")])]})])],"derivedFrom":makeQuery(id+"F5.opExtrude","CAP_EDGE",EDGE,{"disambiguationData":[OSD([subQ0])],"isStart":false})});}
            var Q4;
            {var subQ0=sQuery(id+"F0.wireOp",EDGE,"E25.7");var subQ1=sQuery(id+"F0.wireOp",EDGE,"E25.1");var subQ2=sQuery(id+"F0.wireOp",EDGE,"E25.6");var subQ3=sQuery(id+"F0.wireOp",EDGE,"E25.5");var subQ4=sQuery(id+"F0.wireOp",EDGE,"E25.4");var subQ5=sQuery(id+"F0.wireOp",EDGE,"E25.0");var subQ6=sQuery(id+"F0.wireOp",EDGE,"E25.2");var subQ7=sQuery(id+"F0.wireOp",EDGE,"E25.3");Q4=makeQuery(id+"F8.boolean.opBoolean","INTERSECT",EDGE,{"derivedFrom":[makeQuery(id+"F5.boolean.opBoolean","SPLIT",FACE,{"disambiguationData":[TD([makeQuery(id+"F2.opExtrude","SWEPT_FACE",FACE,{"disambiguationData":[OSD([subQ5])]})])],"derivedFrom":makeQuery(id+"F3.boolean.opBoolean","COPY",FACE,{"derivedFrom":makeQuery(id+"F3.opExtrude","CAP_FACE",FACE,{"disambiguationData":[OSD([subQ5,subQ1,subQ6,subQ7,subQ4,subQ3,subQ2,subQ0])],"isStart":false})})}),makeQuery(id+"F8.opExtrude","SWEPT_FACE",FACE,{"disambiguationData":[OSD([sQuery(id+"F7.wireOp",EDGE,"E67")])]})]});}
            var Q5;
            Q5=makeQuery(id+"F8.boolean.opBoolean","INTERSECT",EDGE,{"disambiguationData":[OD(0.0)],"derivedFrom":[makeQuery(id+"F5.opExtrude","SWEPT_FACE",FACE,{"disambiguationData":[OSD([sQuery(id+"F4.wireOp",EDGE,"E30")])]}),makeQuery(id+"F8.opExtrude","SWEPT_FACE",FACE,{"disambiguationData":[OSD([sQuery(id+"F7.wireOp",EDGE,"E67")])]})]});
            fillet(context, id + "F14", {"entities" : qUnion([Q0, Q1, Q2, Q3, Q4, Q5]), "radius" : 3 * mm, "tangentPropagation" : true, "allowEdgeOverflow" : false});
        }
        {
            var Q0;
            Q0=makeQuery(id+"F1.opExtrude","CAP_EDGE",EDGE,{"disambiguationData":[OSD([sQuery(id+"F0.wireOp",EDGE,"E1.bottom")])],"isStart":false});
            fillet(context, id + "F15", {"entities" : qUnion([Q0]), "radius" : 2 * mm, "tangentPropagation" : true, "allowEdgeOverflow" : false});
        }
        {
            var Q0;
            {var subQ0=sQuery(id+"F0.wireOp",EDGE,"E1.bottom");var subQ1=sQuery(id+"F0.wireOp",EDGE,"E1.top");var subQ2=sQuery(id+"F0.wireOp",EDGE,"E1.left");var subQ3=sQuery(id+"F0.wireOp",EDGE,"E1.right");var subQ4=sQuery(id+"F0.wireOp",EDGE,"E4");var subQ5=sQuery(id+"F0.wireOp",EDGE,"E5");var subQ6=sQuery(id+"F0.wireOp",EDGE,"E6");var subQ7=sQuery(id+"F0.wireOp",EDGE,"E7");var subQ8=sQuery(id+"F0.wireOp",EDGE,"E21.filletArc");var subQ9=sQuery(id+"F0.wireOp",EDGE,"E22.filletArc");var subQ10=sQuery(id+"F0.wireOp",EDGE,"E23.filletArc");var subQ11=sQuery(id+"F0.wireOp",EDGE,"E24.filletArc");Q0=makeQuery(id+"F2.boolean.opBoolean","SPLIT",FACE,{"disambiguationData":[TD([makeQuery(id+"F1.opExtrude","SWEPT_FACE",FACE,{"disambiguationData":[OSD([subQ0])]})])],"derivedFrom":makeQuery(id+"F1.opExtrude","CAP_FACE",FACE,{"disambiguationData":[OSD([subQ0,subQ1,subQ2,subQ3,subQ4,subQ5,subQ6,subQ7,subQ8,subQ9,subQ10,subQ11])],"isStart":true})});}
            var sketch = newSketch(context, id + "F16", { "sketchPlane" : qUnion([Q0])});
            skLineSegment(sketch, "E79.0", {"start": v(24.05, 176.88) * mm, "end": v(152.55, 176.88) * mm});
            skArc(sketch, "E79.1", {"start": v(24.05, 176.88) * mm, "mid": v(16.98, 173.95) * mm, "end": v(14.05, 166.88) * mm});
            skLineSegment(sketch, "E79.2", {"start": v(14.05, 38.38) * mm, "end": v(14.05, 166.88) * mm});
            skArc(sketch, "E79.3", {"start": v(14.05, 38.38) * mm, "mid": v(16.98, 31.31) * mm, "end": v(24.05, 28.38) * mm});
            skLineSegment(sketch, "E79.4", {"start": v(24.05, 28.38) * mm, "end": v(152.55, 28.38) * mm});
            skArc(sketch, "E79.5", {"start": v(152.55, 28.38) * mm, "mid": v(159.62, 31.31) * mm, "end": v(162.55, 38.38) * mm});
            skLineSegment(sketch, "E79.6", {"start": v(162.55, 38.38) * mm, "end": v(162.55, 166.88) * mm});
            skArc(sketch, "E79.7", {"start": v(162.55, 166.88) * mm, "mid": v(159.62, 173.95) * mm, "end": v(152.55, 176.88) * mm});
            skLineSegment(sketch, "E80", {"start": v(88.3, 176.88) * mm, "end": v(88.3, 206.88) * mm, "construction": true});
            skCircle(sketch, "E81", {"center": v(88.3, 206.88) * mm, "radius": 6 * mm});
            skArc(sketch, "E82", {"start": v(73.3, 206.88) * mm, "mid": v(88.3, 221.88) * mm, "end": v(103.3, 206.88) * mm});
            skLineSegment(sketch, "E83", {"start": v(73.3, 206.88) * mm, "end": v(73.3, 194.88) * mm});
            skLineSegment(sketch, "E84", {"start": v(73.3, 194.88) * mm, "end": v(55.3, 176.88) * mm});
            skLineSegment(sketch, "E85", {"start": v(103.3, 206.88) * mm, "end": v(103.3, 191.88) * mm});
            skLineSegment(sketch, "E86", {"start": v(103.3, 191.88) * mm, "end": v(118.3, 176.88) * mm});
            skLineSegment(sketch, "E87", {"start": v(14.05, 102.63) * mm, "end": v(162.55, 102.63) * mm, "construction": true});
            skArc(sketch, "E88.MirrorCS", {"start": v(73.3, -1.62) * mm, "mid": v(88.3, -16.62) * mm, "end": v(103.3, -1.62) * mm});
            skLineSegment(sketch, "E89.MirrorCS", {"start": v(103.3, 13.38) * mm, "end": v(118.3, 28.38) * mm});
            skCircle(sketch, "E90.MirrorC", {"center": v(88.3, -1.62) * mm, "radius": 6 * mm});
            skLineSegment(sketch, "E91.MirrorCS", {"start": v(73.3, -1.62) * mm, "end": v(73.3, 10.38) * mm});
            skLineSegment(sketch, "E92.MirrorCS", {"start": v(73.3, 10.38) * mm, "end": v(55.3, 28.38) * mm});
            skLineSegment(sketch, "E93.MirrorCS", {"start": v(88.3, 28.38) * mm, "end": v(88.3, -1.62) * mm});
            skLineSegment(sketch, "E94.MirrorCS", {"start": v(103.3, -1.62) * mm, "end": v(103.3, 13.38) * mm});
            skSolve(sketch);
        }
        {
            var Q0;
            Q0=makeQuery(id+"F16.imprint","IMPRINT",FACE,{"disambiguationData":[TD([[makeQuery(id+"F16.imprint","IMPRINT",EDGE,{"derivedFrom":sQuery(id+"F16.wireOp",EDGE,"E81")}),-1.0]])]});
            var Q1;
            Q1=makeQuery(id+"F16.imprint","IMPRINT",FACE,{"disambiguationData":[TD([[makeQuery(id+"F16.imprint","IMPRINT",EDGE,{"derivedFrom":sQuery(id+"F16.wireOp",EDGE,"E88.MirrorCS")}),1.0]])]});
            var Q2;
            {var subQ8=sQuery(id+"F16.wireOp",EDGE,"E79.1");Q2=makeQuery(id+"F16.imprint","IMPRINT",FACE,{"disambiguationData":[TD([[makeQuery(id+"F16.imprint","IMPRINT",EDGE,{"derivedFrom":subQ8}),1.0]])]});}
            var Q3;
            Q3=makeQuery(id+"F2.opExtrude","CAP_FACE",FACE,{"disambiguationData":[OSD([sQuery(id+"F0.wireOp",EDGE,"E12"),sQuery(id+"F0.wireOp",EDGE,"E13"),sQuery(id+"F0.wireOp",EDGE,"E14"),sQuery(id+"F0.wireOp",EDGE,"E15"),sQuery(id+"F0.wireOp",EDGE,"E17.filletArc"),sQuery(id+"F0.wireOp",EDGE,"E18.filletArc"),sQuery(id+"F0.wireOp",EDGE,"E19.filletArc"),sQuery(id+"F0.wireOp",EDGE,"E20.filletArc"),sQuery(id+"F0.wireOp",EDGE,"E25.0"),sQuery(id+"F0.wireOp",EDGE,"E25.1"),sQuery(id+"F0.wireOp",EDGE,"E25.2"),sQuery(id+"F0.wireOp",EDGE,"E25.3"),sQuery(id+"F0.wireOp",EDGE,"E25.4"),sQuery(id+"F0.wireOp",EDGE,"E25.5"),sQuery(id+"F0.wireOp",EDGE,"E25.6"),sQuery(id+"F0.wireOp",EDGE,"E25.7")])],"isStart":false});
            extrude(context, id + "F17", {"entities" : qUnion([Q0, Q1, Q2]), "operationType" : NewBodyOperationType.ADD, "endBound" : BoundingType.UP_TO_SURFACE, "endBoundEntityFace" : qUnion([Q3]), "depth" : 25 * mm});
        }
    });
